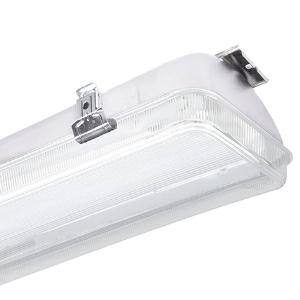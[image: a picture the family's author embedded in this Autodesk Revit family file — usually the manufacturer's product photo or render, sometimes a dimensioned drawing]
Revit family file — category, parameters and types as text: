
# Revit family: 3f_filippi_-_beta_235_75_pc_ampio_3f_filippi_-_52888_-_beta_235_led_752x45_dali_ampio_l1265
name_source: partatom
category: Lighting Fixtures
units: mm (PartAtom-declared; Revit-internal decimal feet)

## family parameters
Cut with Voids When Loaded = No
Host = Face
Light Source = No
Part Type = Normal
Room Calculation Point = No
Round Connector Dimension = Use Diameter
Shared = No

## types (1)
- 3F Filippi - Beta 235 75 PC Ampio (1 x LED, 14369 lm, 92 W, 4000 K)
    Apparent Load = 92 VA
    Approval mark = CE
    CIE Flux Codes = 59 89 98 98 100
    Color Rendering = 80
    Color Temperature = 4000 K
    Control Gear = Electronic transformer
    Default Elevation = 1800 mm
    Description = ILLUMINOTECHNICAL
Luminous efficiency 100% (DLOR 99%, ULOR 1%).
Initial luminous flux of the luminaire 14369 lm.
Wide symmetric distribution.
Installation Interdistance Transv.D = 1.40 x hu - Long.D = 1.43 x hu.
Tabular UGR (CIE 117 - 4H-8H; S=0.25H; 70/50/20): RUG 21.3 - 21.9.
Beam angle: 98° - 100°.
Luminous efficacy 156 lm/W.
Lifetime (L93/B10): 30000 h. (tq+25°C)
Lifetime (L90/B10): 50000 h. (tq+25°C)
Lifetime (L85/B10): 80000 h. (tq+25°C)
Lifetime (L80/B10): 100000 h. (tq+25°C)
Lifetime (L85/B10): 50000 h. (tq+45°C)
Sudden decreased luminous flux after 50000 hours: 0% (C0).
Photobiological safety in compliance with IEC/TR 62778: RG0 risk exempt, (IEC 62471).
In compliance with IEC/EN 62722-2-1 - IEC/EN 62717 standards.

SOURCE
2 linear LED modules 45W/840.
Energy efficiency class (UE 2019/2020 - UE 2019/2015): C.
CIE 13.3 Colour rendering index: CRI >80 (R9 <50%).
IES TM-30 Fidelity Index: Rf = 84 Rg = 95.
CCT nominal colour temperature 4000 K.
Colour initial tolerance (MacAdam): SDCM 3.

MECHANICAL
Single-piece housing in pressed steel, powder-coated in white epoxy-polyester.
Polycarbonate screen etched internally, V2 self-extinguishing, UV stabilised, injection moulded.
Ecologic anti-aging injected sealing gasket.
Oversized gear-tray reflector unit in highly reflective white painted hot-galvanised steel.
Methacrylate (PMMA) lenses with external flat surface.
Galvanised steel snap-lock clips for diffuser mounting (safety n° 4 per fixture).
Luminaire with limited surface temperature. - D - (EN 60598-2-24)
Dimensions: 1265x235 mm, height 135 mm. Weight 7.575 kg.
IP65 protection degree.
Mechanical strength to impacts IK10 (20 joule).
Glow-wire test resistance 850°C.

ELECTRICAL
Halogen Free DALI-2 DATI (Parts 251, 252, 253), PUSH-DIM, electronic wiring 230V-50/60Hz, power factor 0.95 at full load, THD <25%, constant output current, class I, 1 driver, 1 DALI addresse.
Power of the luminaire 92 W.
ENEC - CE.
Flicker: <4%.
Luminaire compliant with EN 60598-2-22 for power supply from a centralised emergency system CPSS (Central Power Supply System), not incorporated in the luminaire - high risk areas excluded. The default power and flux are 100% in AC and 15% in DC.
Ambient temperature from -20°C to +45°C.
Temperature class T6 max 85°C.
Quick connection via M25 5P connector with 9-13 mm tightening range.
Relative humidity UR: <85%.

INSTALLATION
Ceiling / Suspended / Wall.
All accessories dedicated to this product are available on the Catalog and on our website www.3F-Filippi.com.

APPLICATIONS
Suitable product for food production plants (HACCP), IFS (Food Version 6), BRC (GSFS Food Version 7).
Dry, dusty indoor environments, subject to occasional water splashes.
Industrial environments, warehouses, environments where security locks are required on all clips, e.g. prisons (on request).
Environments in which it is necessary a total protection against falling fragments (eg environments with foodstuffs or machines with moving parts or with extreme temperature changes), use luminaires with laminated glass.
Tempered glass is not immune to falling fragments from harmless and caused by shocks or exceptionally derived from the tempering process.

LIGHT MANAGEMENT
Recommended minimum setting: 10%.
The luminaire, equipped with (DALI-2 DATI) driver, can be controlled manually with 3F Easy Dim technology or automatically/manually with wired or wireless DALI/D2D control systems.
The D2D driver guarantees interoperability with other devices with the same certification by making the following information available:
Device Data (Part 251), Energy Report (Part 252), Diagnosis & Maintenance (Part 253).
In electrical systems without a regulation system (manual or automatic) and DALI bus, a suitable jumper must be made on the DA-DA terminals of the appliance.

WARNING
Fixture not suitable for cold stores with an ambient temperature <0°C and/or relative humidity >85%.
Luminaire designed for disposal/recycling at end-of-life.
Replaceable (LED only) light source by a professional. Replaceable control gear by a professional.
    Height = 135 mm
    Lamp = 1 x LED
    Lamp Light Flux = 14369 lm
    Lamp Power = 92 W
    Lamp count = 1
    Length = 1265 mm
    Lifetime = 50000 h
    Luminous efficacy = 156 lm/W
    Manufacturer = 3F Filippi
    ModVariant = No
    Model = 3F Filippi - 52888 - Beta 235 LED 752x45 DALI AMPIO L1265
    Mounting Place = Ceiling
    Mounting Type = Pendant
    Number of Poles = 1
    OnlyDefault = Yes
    Power Factor = 1
    Product Name = 3F Filippi - Beta 235 75 PC Ampio
    Product group = pendant luminaire
    ProductGroupID = 9
    Protection Class = Protection class I
    Protection Degree = IP 65
    RLX_Detail_Level = 1
    RLX_Emergency_Light_Flux = 0 lm
    RLX_Emergency_Type = 0
    RLX_Emergency_Type_DB = No
    RlxData = <blob elided: 92217 chars, md5=e3c086fd>
    Socket = socket
    Standby Power = 0 W
    System Light Flux = 14369 lm
    System Power = 92 W
    Type Comments = Product without accessories
    Type Image = 3ffilippi_52888.jpg
    URL = http://relux.com
    VarID = ---
    Voltage = 0 V
    Weight = 0.00 kg
    Width = 235 mm

## geometry (parser evidence)
native form markers: Blend x4, Sweep x11
no freeform markers — native parametric forms only
